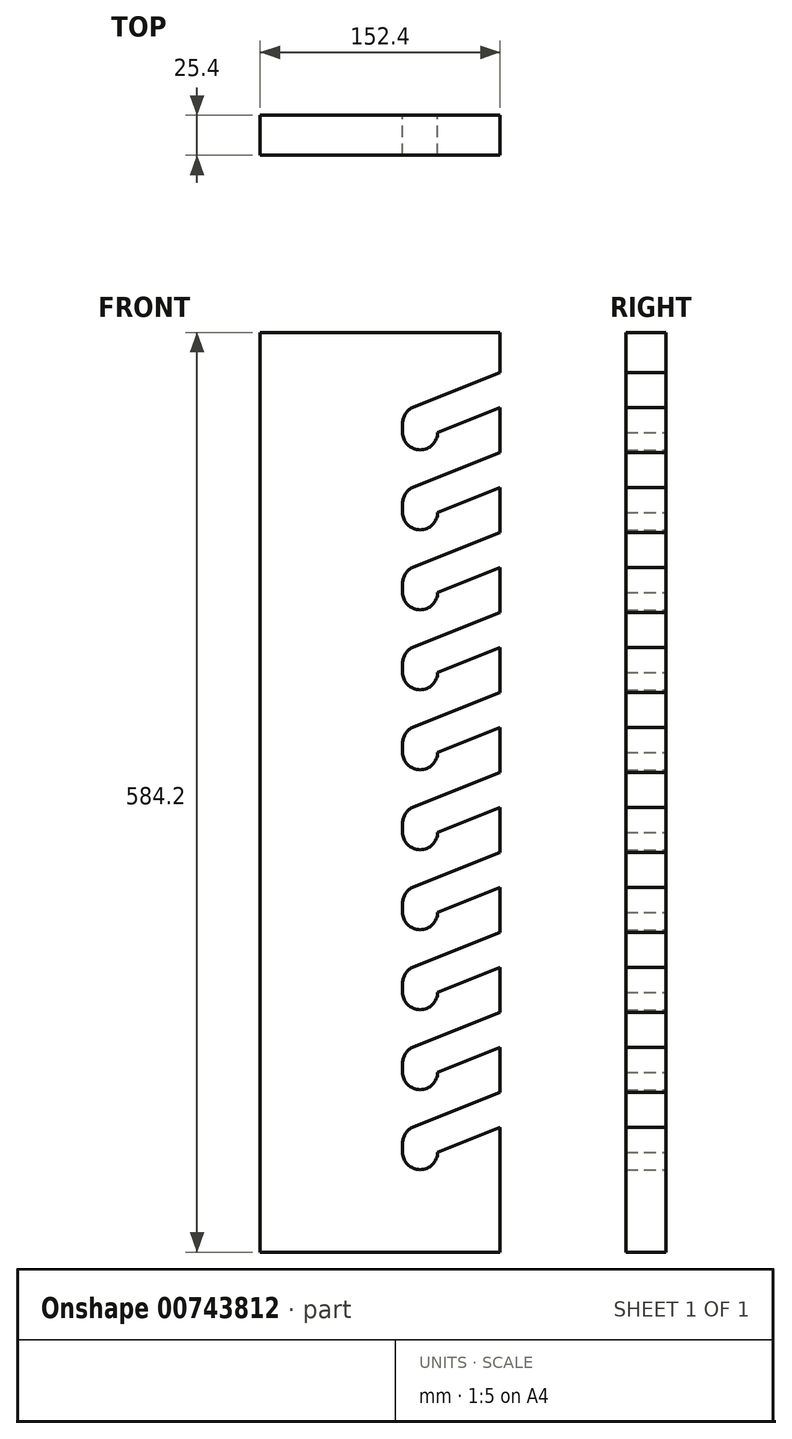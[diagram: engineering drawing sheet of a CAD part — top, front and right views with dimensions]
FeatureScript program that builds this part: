
annotation { "Feature Type Name" : "Feature", "Feature Type Description" : "" }
export const myFeature = defineFeature(function(context is Context, id is Id, definition is map)
    precondition{}
    {
        {
            var Q0;
            Q0=qCreatedBy(makeId("Front.planeOp"),FACE);
            var sketch = newSketch(context, id + "F0", { "sketchPlane" : qUnion([Q0])});
            skLineSegment(sketch, "E0.bottom", {"start": v(76.2, 292.1) * mm, "end": v(-76.2, 292.1) * mm});
            skLineSegment(sketch, "E0.top", {"start": v(76.2, -292.1) * mm, "end": v(-76.2, -292.1) * mm});
            skLineSegment(sketch, "E0.left", {"start": v(76.2, 292.1) * mm, "end": v(76.2, -292.1) * mm});
            skLineSegment(sketch, "E0.right", {"start": v(-76.2, 292.1) * mm, "end": v(-76.2, -292.1) * mm});
            skArc(sketch, "E1", {"start": v(36.51, 234.41) * mm, "mid": v(25.4, 245.52) * mm, "end": v(14.29, 234.41) * mm});
            skArc(sketch, "E2", {"start": v(14.29, 228.6) * mm, "mid": v(25.4, 217.49) * mm, "end": v(36.51, 228.6) * mm});
            skLineSegment(sketch, "E3", {"start": v(14.29, 234.41) * mm, "end": v(14.29, 228.6) * mm});
            skLineSegment(sketch, "E4", {"start": v(36.51, 234.41) * mm, "end": v(36.51, 228.6) * mm});
            skLineSegment(sketch, "E5", {"start": v(36.51, 228.6) * mm, "end": v(76.2, 244.48) * mm});
            skLineSegment(sketch, "E6", {"start": v(21.27, 244.73) * mm, "end": v(76.2, 266.7) * mm});
            skLineSegment(sketch, "E7.0.1.0", {"start": v(21.27, 193.93) * mm, "end": v(76.2, 215.9) * mm});
            skLineSegment(sketch, "E7.0.1.1", {"start": v(36.51, 177.8) * mm, "end": v(76.2, 193.68) * mm});
            skArc(sketch, "E7.0.1.2", {"start": v(36.51, 183.61) * mm, "mid": v(25.4, 194.72) * mm, "end": v(14.29, 183.61) * mm});
            skLineSegment(sketch, "E7.0.1.3", {"start": v(14.29, 183.61) * mm, "end": v(14.29, 177.8) * mm});
            skLineSegment(sketch, "E7.0.1.4", {"start": v(36.51, 183.61) * mm, "end": v(36.51, 177.8) * mm});
            skArc(sketch, "E7.0.1.5", {"start": v(14.29, 177.8) * mm, "mid": v(25.4, 166.69) * mm, "end": v(36.51, 177.8) * mm});
            skLineSegment(sketch, "E7.0.2.0", {"start": v(21.27, 143.13) * mm, "end": v(76.2, 165.1) * mm});
            skLineSegment(sketch, "E7.0.2.1", {"start": v(36.51, 127) * mm, "end": v(76.2, 142.88) * mm});
            skArc(sketch, "E7.0.2.2", {"start": v(36.51, 132.81) * mm, "mid": v(25.4, 143.92) * mm, "end": v(14.29, 132.81) * mm});
            skLineSegment(sketch, "E7.0.2.3", {"start": v(14.29, 132.81) * mm, "end": v(14.29, 127) * mm});
            skLineSegment(sketch, "E7.0.2.4", {"start": v(36.51, 132.81) * mm, "end": v(36.51, 127) * mm});
            skArc(sketch, "E7.0.2.5", {"start": v(14.29, 127) * mm, "mid": v(25.4, 115.89) * mm, "end": v(36.51, 127) * mm});
            skLineSegment(sketch, "E7.0.3.0", {"start": v(21.27, 92.33) * mm, "end": v(76.2, 114.3) * mm});
            skLineSegment(sketch, "E7.0.3.1", {"start": v(36.51, 76.2) * mm, "end": v(76.2, 92.08) * mm});
            skArc(sketch, "E7.0.3.2", {"start": v(36.51, 82.01) * mm, "mid": v(25.4, 93.12) * mm, "end": v(14.29, 82.01) * mm});
            skLineSegment(sketch, "E7.0.3.3", {"start": v(14.29, 82.01) * mm, "end": v(14.29, 76.2) * mm});
            skLineSegment(sketch, "E7.0.3.4", {"start": v(36.51, 82.01) * mm, "end": v(36.51, 76.2) * mm});
            skArc(sketch, "E7.0.3.5", {"start": v(14.29, 76.2) * mm, "mid": v(25.4, 65.09) * mm, "end": v(36.51, 76.2) * mm});
            skLineSegment(sketch, "E7.0.4.0", {"start": v(21.27, 41.53) * mm, "end": v(76.2, 63.5) * mm});
            skLineSegment(sketch, "E7.0.4.1", {"start": v(36.51, 25.4) * mm, "end": v(76.2, 41.28) * mm});
            skArc(sketch, "E7.0.4.2", {"start": v(36.51, 31.21) * mm, "mid": v(25.4, 42.32) * mm, "end": v(14.29, 31.21) * mm});
            skLineSegment(sketch, "E7.0.4.3", {"start": v(14.29, 31.21) * mm, "end": v(14.29, 25.4) * mm});
            skLineSegment(sketch, "E7.0.4.4", {"start": v(36.51, 31.21) * mm, "end": v(36.51, 25.4) * mm});
            skArc(sketch, "E7.0.4.5", {"start": v(14.29, 25.4) * mm, "mid": v(25.4, 14.29) * mm, "end": v(36.51, 25.4) * mm});
            skLineSegment(sketch, "E7.0.5.0", {"start": v(21.27, -9.27) * mm, "end": v(76.2, 12.7) * mm});
            skLineSegment(sketch, "E7.0.5.1", {"start": v(36.51, -25.4) * mm, "end": v(76.2, -9.52) * mm});
            skArc(sketch, "E7.0.5.2", {"start": v(36.51, -19.59) * mm, "mid": v(25.4, -8.48) * mm, "end": v(14.29, -19.59) * mm});
            skLineSegment(sketch, "E7.0.5.3", {"start": v(14.29, -19.59) * mm, "end": v(14.29, -25.4) * mm});
            skLineSegment(sketch, "E7.0.5.4", {"start": v(36.51, -19.59) * mm, "end": v(36.51, -25.4) * mm});
            skArc(sketch, "E7.0.5.5", {"start": v(14.29, -25.4) * mm, "mid": v(25.4, -36.51) * mm, "end": v(36.51, -25.4) * mm});
            skLineSegment(sketch, "E7.0.6.0", {"start": v(21.27, -60.07) * mm, "end": v(76.2, -38.1) * mm});
            skLineSegment(sketch, "E7.0.6.1", {"start": v(36.51, -76.2) * mm, "end": v(76.2, -60.33) * mm});
            skArc(sketch, "E7.0.6.2", {"start": v(36.51, -70.39) * mm, "mid": v(25.4, -59.28) * mm, "end": v(14.29, -70.39) * mm});
            skLineSegment(sketch, "E7.0.6.3", {"start": v(14.29, -70.39) * mm, "end": v(14.29, -76.2) * mm});
            skLineSegment(sketch, "E7.0.6.4", {"start": v(36.51, -70.39) * mm, "end": v(36.51, -76.2) * mm});
            skArc(sketch, "E7.0.6.5", {"start": v(14.29, -76.2) * mm, "mid": v(25.4, -87.31) * mm, "end": v(36.51, -76.2) * mm});
            skLineSegment(sketch, "E7.0.7.0", {"start": v(21.27, -110.87) * mm, "end": v(76.2, -88.9) * mm});
            skLineSegment(sketch, "E7.0.7.1", {"start": v(36.51, -127) * mm, "end": v(76.2, -111.13) * mm});
            skArc(sketch, "E7.0.7.2", {"start": v(36.51, -121.19) * mm, "mid": v(25.4, -110.08) * mm, "end": v(14.29, -121.19) * mm});
            skLineSegment(sketch, "E7.0.7.3", {"start": v(14.29, -121.19) * mm, "end": v(14.29, -127) * mm});
            skLineSegment(sketch, "E7.0.7.4", {"start": v(36.51, -121.19) * mm, "end": v(36.51, -127) * mm});
            skArc(sketch, "E7.0.7.5", {"start": v(14.29, -127) * mm, "mid": v(25.4, -138.11) * mm, "end": v(36.51, -127) * mm});
            skLineSegment(sketch, "E7.0.8.0", {"start": v(21.27, -161.67) * mm, "end": v(76.2, -139.7) * mm});
            skLineSegment(sketch, "E7.0.8.1", {"start": v(36.51, -177.8) * mm, "end": v(76.2, -161.93) * mm});
            skArc(sketch, "E7.0.8.2", {"start": v(36.51, -171.99) * mm, "mid": v(25.4, -160.88) * mm, "end": v(14.29, -171.99) * mm});
            skLineSegment(sketch, "E7.0.8.3", {"start": v(14.29, -171.99) * mm, "end": v(14.29, -177.8) * mm});
            skLineSegment(sketch, "E7.0.8.4", {"start": v(36.51, -171.99) * mm, "end": v(36.51, -177.8) * mm});
            skArc(sketch, "E7.0.8.5", {"start": v(14.29, -177.8) * mm, "mid": v(25.4, -188.91) * mm, "end": v(36.51, -177.8) * mm});
            skLineSegment(sketch, "E7.0.9.0", {"start": v(21.27, -212.47) * mm, "end": v(76.2, -190.5) * mm});
            skLineSegment(sketch, "E7.0.9.1", {"start": v(36.51, -228.6) * mm, "end": v(76.2, -212.73) * mm});
            skArc(sketch, "E7.0.9.2", {"start": v(36.51, -222.79) * mm, "mid": v(25.4, -211.68) * mm, "end": v(14.29, -222.79) * mm});
            skLineSegment(sketch, "E7.0.9.3", {"start": v(14.29, -222.79) * mm, "end": v(14.29, -228.6) * mm});
            skLineSegment(sketch, "E7.0.9.4", {"start": v(36.51, -222.79) * mm, "end": v(36.51, -228.6) * mm});
            skArc(sketch, "E7.0.9.5", {"start": v(14.29, -228.6) * mm, "mid": v(25.4, -239.71) * mm, "end": v(36.51, -228.6) * mm});
            skLineSegment(sketch, "E7.direction1", {"start": v(21.27, 244.73) * mm, "end": v(46.67, 244.73) * mm, "construction": true});
            skLineSegment(sketch, "E7.direction2", {"start": v(21.27, 244.73) * mm, "end": v(21.27, 193.93) * mm, "construction": true});
            skSolve(sketch);
        }
        {
            var Q0;
            {var subQ3=sQuery(id+"F0.wireOp",EDGE,"E0.bottom");Q0=makeQuery(id+"F0.imprint","IMPRINT",FACE,{"disambiguationData":[TD([[makeQuery(id+"F0.imprint","IMPRINT",EDGE,{"derivedFrom":subQ3}),1.0]])]});}
            extrude(context, id + "F1", {"entities" : qUnion([Q0]), "depth" : 25.4 * mm, "offsetDistance" : 25.4 * mm});
        }
    });
